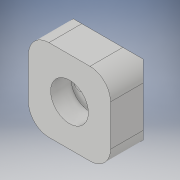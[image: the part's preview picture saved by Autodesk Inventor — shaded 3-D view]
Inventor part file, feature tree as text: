
AUTODESK INVENTOR PART (.ipt)
format: ipt  version: 2017 SP1 (Build 210196100, 196)  size: 142,848 bytes
history: native  units: in
note: dims shown in document units (in); Inventor stores cm internally (conversion verified against a paired STEP export)
features: sketch x3, extrude x2, hole x1, chamfer x1, fillet x1
ambient origin geometry x8: Origin, YZ Plane, XZ Plane, XY Plane, X Axis, Y Axis, Z Axis, Center Point
bodies: Solid1 (feature_tree)
feature tree (8):
  extrude  "Extrusion1"  Depth=0.5in
  extrude  "Extrusion2"  Depth=0.25in
  hole  "Hole1"  [1 undecoded]
  chamfer  "Chamfer2"  Distance=0.05in
  fillet  "Fillet1"  Radius=0.0625in
  sketch  "Sketch1"  dims[d0=0.5in d1=0.5in]
  sketch  "Sketch2"  dims[d2=0.25in d3=0.0in d4=0.23in]
  sketch  "Sketch3"  dims[d5=0.125in d6=0.0in d7=0.05in d8=0.05in d9=0.0625in d10=0.0625in d11=0.075in d12=0.075in d13=0.75in d14=0.375in d15=0.25in d16=0.5635in d17=1.0in d18=0.8108in d22=0.05in d23=0.125in d24=45.0deg d25=0.125in d26=0.125in]
note: 1 required parameter value undecoded (feature->parameter linkage not recoverable at this tier; creation-order binding heuristic only, values carry confidence <= 0.55)
